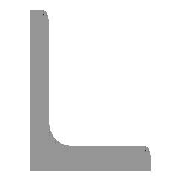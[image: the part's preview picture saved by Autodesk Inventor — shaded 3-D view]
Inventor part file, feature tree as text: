
AUTODESK INVENTOR PART (.ipt)
format: ipt  version: 2016 (Build 200138000, 138)  size: 119,296 bytes
history: native  units: mm (DEFAULTED — no unit token found)
features: other x4, sketch x2, extrude x1, plane x1
ambient origin geometry x8: Origin, YZ Plane, XZ Plane, XY Plane, X Axis, Y Axis, Z Axis, Center Point
bodies: Solid1 (feature_tree)
feature tree (8):
  parser-record x1  (decoder bookkeeping rows leaked as tree rows — omitted from the tree; the rows remain in map.json)
  other  "Driven Length"
  other  "Plano inicial"
  other  "Plano final"
  extrude  "Cuerpo"  Depth=38.1mm
  sketch  "Sketch3"  dims[d0=38.1mm d1=38.1mm]
  plane  "Work Plane3"
  sketch  "Sketch4"  dims[d2=4.7625mm d3=4.7625mm d4=2400.0mm d5=0.0mm d10=0.0mm d11=0.0mm d12=-0.0mm d13=2400.0mm d14=4.826mm d15=2.286mm d16=90.0deg d17=2400.0mm]
